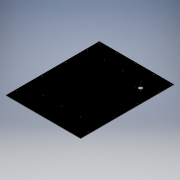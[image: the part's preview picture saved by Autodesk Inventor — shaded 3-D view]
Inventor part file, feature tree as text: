
AUTODESK INVENTOR PART (.ipt)
format: ipt  version: 2017.3 (Build 213256000, 256)  size: 161,280 bytes
history: native  units: mm
features: sheet_metal_op x1, sketch x1, other x1
ambient origin geometry x8: Origin, YZ Plane, XZ Plane, XY Plane, X Axis, Y Axis, Z Axis, Center Point
bodies: Body1 (feature_tree)
feature tree (3):
  sheet_metal_op  "Face3"
  sketch  "Sketch1"  dims[d0=440.0mm d1=550.0mm d2=10.0mm d3=10.0mm d4=10.0mm d5=110.0mm d6=80.0mm d7=110.0mm d8=110.0mm d9=70.0mm d10=55.0mm d11=4.2mm d12=1.5mm d13=1.5mm d14=42.0mm d15=15.0mm d16=50.0mm d17=31.0mm d18=3.4mm d19=22.0mm d20=1.5mm]
  other  "Plate3"
